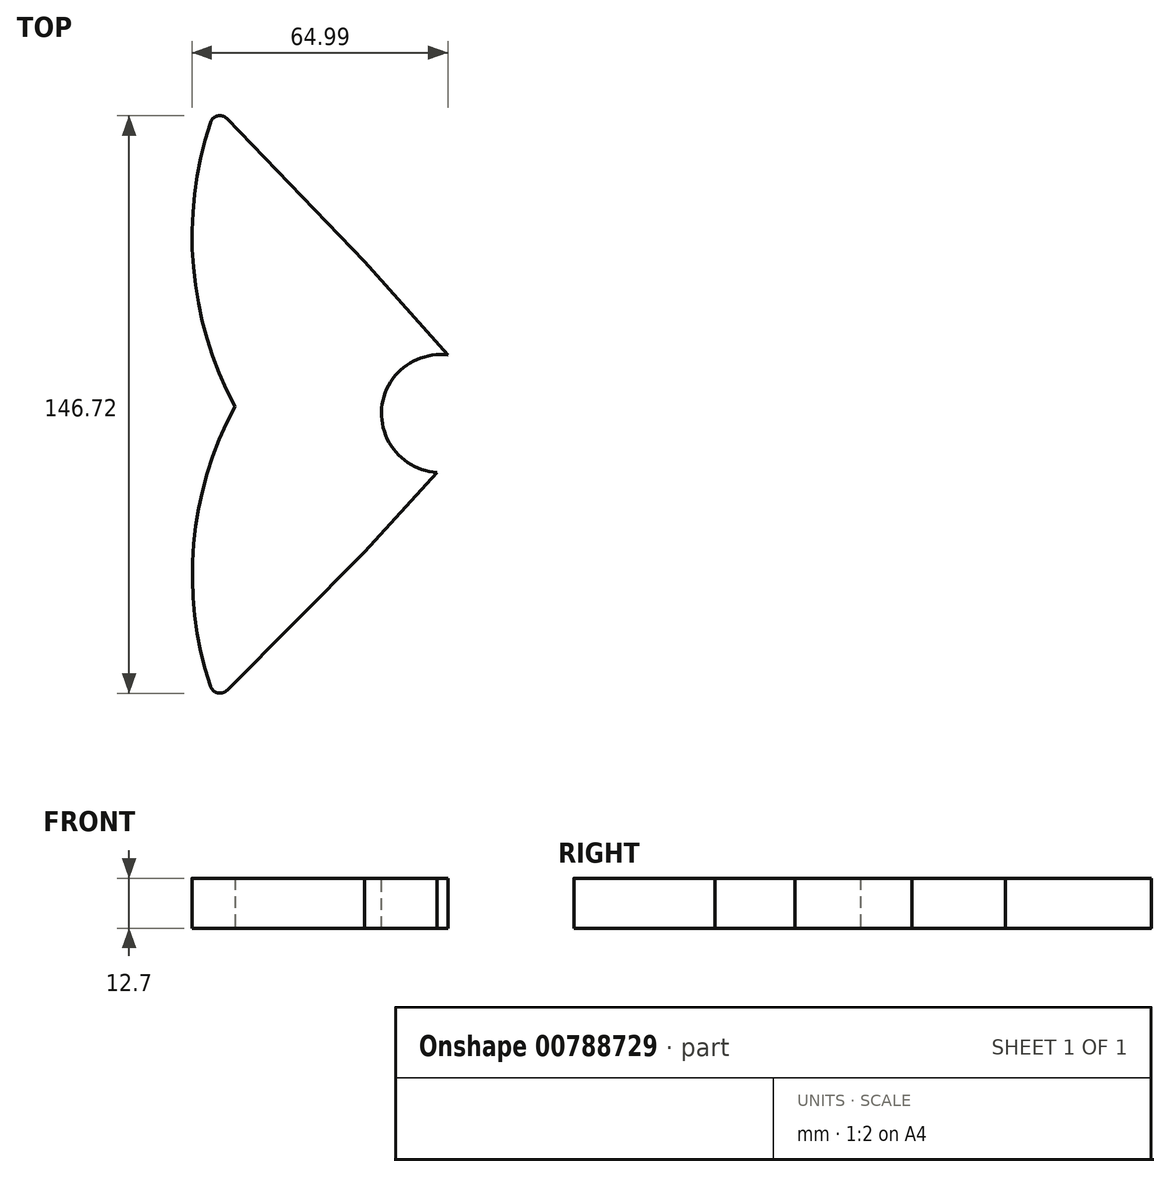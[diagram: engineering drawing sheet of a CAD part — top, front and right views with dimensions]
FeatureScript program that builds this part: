
annotation { "Feature Type Name" : "Feature", "Feature Type Description" : "" }
export const myFeature = defineFeature(function(context is Context, id is Id, definition is map)
    precondition{}
    {
        {
            var Q0;
            Q0=qCreatedBy(makeId("Top.planeOp"),FACE);
            var sketch = newSketch(context, id + "F0", { "sketchPlane" : qUnion([Q0])});
            skArc(sketch, "E0", {"start": v(21.12, 13.08) * mm, "mid": v(24.74, -2.27) * mm, "end": v(18.39, -16.7) * mm});
            skLineSegment(sketch, "E1", {"start": v(18.39, -16.7) * mm, "end": v(0, -36.94) * mm});
            skLineSegment(sketch, "E2", {"start": v(21.12, 13.08) * mm, "end": v(0, 36.82) * mm});
            skLineSegment(sketch, "E3", {"start": v(0, -36.94) * mm, "end": v(-37.82, -74.93) * mm});
            skLineSegment(sketch, "E4", {"start": v(0, 36.82) * mm, "end": v(-37.82, 76.07) * mm});
            skPoint(sketch, "E5", {"position": v(-33, 0) * mm});
            skArc(sketch, "E6", {"start": v(-37.82, 76.07) * mm, "mid": v(-43.69, 37.5) * mm, "end": v(-33, 0) * mm});
            skArc(sketch, "E7", {"start": v(-33, 0) * mm, "mid": v(-43.61, -36.94) * mm, "end": v(-37.82, -74.93) * mm});
            skSolve(sketch);
        }
        {
            var Q0;
            Q0 = qSketchRegion(id + "F0", true);
            extrude(context, id + "F1", {"entities" : qUnion([Q0]), "depth" : 12.7 * mm, "offsetDistance" : 25.4 * mm});
        }
        {
            var Q0;
            Q0=makeQuery(id+"F1.opExtrude","SWEPT_EDGE",EDGE,{"disambiguationData":[OSD([sQuery(id+"F0.wireOp",EDGE,"E3"),sQuery(id+"F0.wireOp",EDGE,"E7")])]});
            var Q1;
            Q1=makeQuery(id+"F1.opExtrude","SWEPT_EDGE",EDGE,{"disambiguationData":[OSD([sQuery(id+"F0.wireOp",EDGE,"E4"),sQuery(id+"F0.wireOp",EDGE,"E6")])]});
            fillet(context, id + "F2", {"entities" : qUnion([Q0, Q1]), "radius" : 2.54 * mm, "tangentPropagation" : true, "allowEdgeOverflow" : false});
        }
        {
            var Q0;
            Q0=makeQuery(id+"F1.opExtrude","CAP_FACE",FACE,{"disambiguationData":[OSD([sQuery(id+"F0.wireOp",EDGE,"E0"),sQuery(id+"F0.wireOp",EDGE,"E1"),sQuery(id+"F0.wireOp",EDGE,"E2"),sQuery(id+"F0.wireOp",EDGE,"E3"),sQuery(id+"F0.wireOp",EDGE,"E4"),sQuery(id+"F0.wireOp",EDGE,"E6"),sQuery(id+"F0.wireOp",EDGE,"E7")])],"isStart":false});
            var sketch = newSketch(context, id + "F3", { "sketchPlane" : qUnion([Q0])});
            skArc(sketch, "E8", {"start": v(21.12, 13.08) * mm, "mid": v(4.33, -0.4) * mm, "end": v(18.39, -16.7) * mm});
            skSolve(sketch);
        }
        {
            var Q0;
            Q0=makeQuery(id+"F3.imprint","IMPRINT",FACE,{"disambiguationData":[TD([[makeQuery(id+"F3.imprint","IMPRINT",EDGE,{"derivedFrom":sQuery(id+"F3.wireOp",EDGE,"E8")}),1.0]])]});
            extrude(context, id + "F4", {"entities" : qUnion([Q0]), "operationType" : NewBodyOperationType.REMOVE, "oppositeDirection" : true, "depth" : 25.4 * mm, "offsetDistance" : 25.4 * mm});
        }
    });
